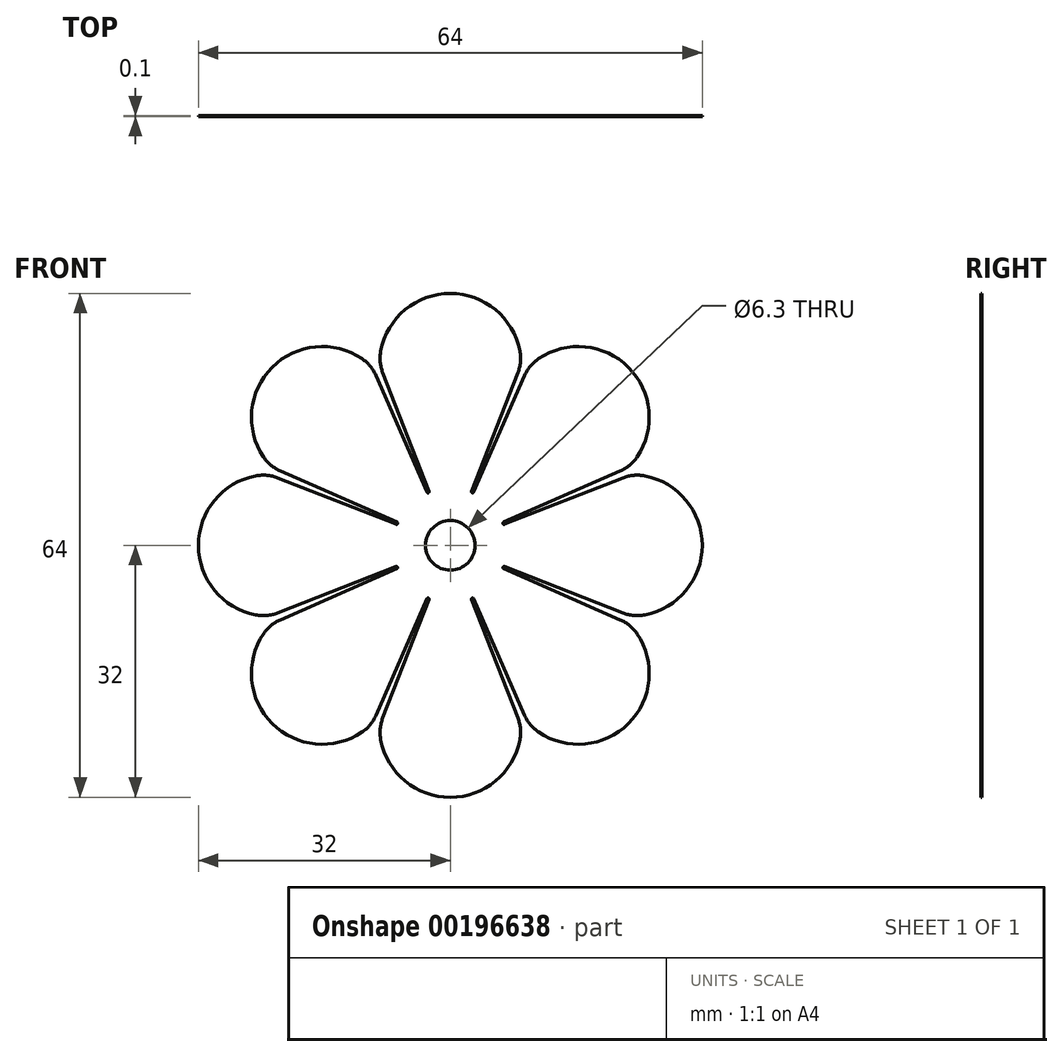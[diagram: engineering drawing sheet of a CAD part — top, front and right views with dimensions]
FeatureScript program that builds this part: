
annotation { "Feature Type Name" : "Feature", "Feature Type Description" : "" }
export const myFeature = defineFeature(function(context is Context, id is Id, definition is map)
    precondition{}
    {
        {
            var Q0;
            Q0=qCreatedBy(makeId("Front.planeOp"),FACE);
            var sketch = newSketch(context, id + "F0", { "sketchPlane" : qUnion([Q0])});
            skCircle(sketch, "E0", {"center": v(0, 0) * mm, "radius": 3.15 * mm});
            skArc(sketch, "E1", {"start": v(-2.77, 6.7) * mm, "mid": v(-2.77, 6.7) * mm, "end": v(-2.78, 6.7) * mm});
            skArc(sketch, "E2", {"start": v(-8.84, 24.7) * mm, "mid": v(0, 32) * mm, "end": v(8.84, 24.7) * mm});
            skLineSegment(sketch, "E3", {"start": v(0, 0) * mm, "end": v(1.15, 2.93) * mm});
            skPoint(sketch, "E4.visualSharp", {"position": v(-9, 23) * mm});
            skArc(sketch, "E4.filletArc", {"start": v(-8.84, 24.7) * mm, "mid": v(-8.9, 23.3) * mm, "end": v(-8.58, 21.94) * mm});
            skPoint(sketch, "E5.visualSharp", {"position": v(9, 23) * mm});
            skArc(sketch, "E5.filletArc", {"start": v(8.58, 21.94) * mm, "mid": v(8.9, 23.3) * mm, "end": v(8.84, 24.7) * mm});
            skLineSegment(sketch, "E6.trimOffspring", {"start": v(-2.7, 6.88) * mm, "end": v(-8.58, 21.94) * mm});
            skLineSegment(sketch, "E7.trimOffspring", {"start": v(2.7, 6.88) * mm, "end": v(8.58, 21.94) * mm});
            skLineSegment(sketch, "E8.1.0", {"start": v(-6.77, 2.96) * mm, "end": v(-21.58, 9.44) * mm});
            skArc(sketch, "E8.1.1", {"start": v(-23.72, 11.22) * mm, "mid": v(-22.78, 10.18) * mm, "end": v(-21.58, 9.44) * mm});
            skArc(sketch, "E8.1.2", {"start": v(-23.72, 11.22) * mm, "mid": v(-22.63, 22.63) * mm, "end": v(-11.22, 23.72) * mm});
            skArc(sketch, "E8.1.3", {"start": v(-9.44, 21.58) * mm, "mid": v(-10.18, 22.78) * mm, "end": v(-11.22, 23.72) * mm});
            skLineSegment(sketch, "E8.1.4", {"start": v(-2.96, 6.77) * mm, "end": v(-9.44, 21.58) * mm});
            skLineSegment(sketch, "E8.2.0", {"start": v(-6.88, -2.7) * mm, "end": v(-21.94, -8.58) * mm});
            skArc(sketch, "E8.2.1", {"start": v(-24.7, -8.84) * mm, "mid": v(-23.3, -8.9) * mm, "end": v(-21.94, -8.58) * mm});
            skArc(sketch, "E8.2.2", {"start": v(-24.7, -8.84) * mm, "mid": v(-32, 0) * mm, "end": v(-24.7, 8.84) * mm});
            skArc(sketch, "E8.2.3", {"start": v(-21.94, 8.58) * mm, "mid": v(-23.3, 8.9) * mm, "end": v(-24.7, 8.84) * mm});
            skLineSegment(sketch, "E8.2.4", {"start": v(-6.88, 2.7) * mm, "end": v(-21.94, 8.58) * mm});
            skLineSegment(sketch, "E8.3.0", {"start": v(-2.96, -6.77) * mm, "end": v(-9.44, -21.58) * mm});
            skArc(sketch, "E8.3.1", {"start": v(-11.22, -23.72) * mm, "mid": v(-10.18, -22.78) * mm, "end": v(-9.44, -21.58) * mm});
            skArc(sketch, "E8.3.2", {"start": v(-11.22, -23.72) * mm, "mid": v(-22.63, -22.63) * mm, "end": v(-23.72, -11.22) * mm});
            skArc(sketch, "E8.3.3", {"start": v(-21.58, -9.44) * mm, "mid": v(-22.78, -10.18) * mm, "end": v(-23.72, -11.22) * mm});
            skLineSegment(sketch, "E8.3.4", {"start": v(-6.77, -2.96) * mm, "end": v(-21.58, -9.44) * mm});
            skLineSegment(sketch, "E8.4.0", {"start": v(2.7, -6.88) * mm, "end": v(8.58, -21.94) * mm});
            skArc(sketch, "E8.4.1", {"start": v(8.84, -24.7) * mm, "mid": v(8.9, -23.3) * mm, "end": v(8.58, -21.94) * mm});
            skArc(sketch, "E8.4.2", {"start": v(8.84, -24.7) * mm, "mid": v(0, -32) * mm, "end": v(-8.84, -24.7) * mm});
            skArc(sketch, "E8.4.3", {"start": v(-8.58, -21.94) * mm, "mid": v(-8.9, -23.3) * mm, "end": v(-8.84, -24.7) * mm});
            skLineSegment(sketch, "E8.4.4", {"start": v(-2.7, -6.88) * mm, "end": v(-8.58, -21.94) * mm});
            skLineSegment(sketch, "E8.5.0", {"start": v(6.77, -2.96) * mm, "end": v(21.58, -9.44) * mm});
            skArc(sketch, "E8.5.1", {"start": v(23.72, -11.22) * mm, "mid": v(22.78, -10.18) * mm, "end": v(21.58, -9.44) * mm});
            skArc(sketch, "E8.5.2", {"start": v(23.72, -11.22) * mm, "mid": v(22.63, -22.63) * mm, "end": v(11.22, -23.72) * mm});
            skArc(sketch, "E8.5.3", {"start": v(9.44, -21.58) * mm, "mid": v(10.18, -22.78) * mm, "end": v(11.22, -23.72) * mm});
            skLineSegment(sketch, "E8.5.4", {"start": v(2.96, -6.77) * mm, "end": v(9.44, -21.58) * mm});
            skLineSegment(sketch, "E8.6.0", {"start": v(6.88, 2.7) * mm, "end": v(21.94, 8.58) * mm});
            skArc(sketch, "E8.6.1", {"start": v(24.7, 8.84) * mm, "mid": v(23.3, 8.9) * mm, "end": v(21.94, 8.58) * mm});
            skArc(sketch, "E8.6.2", {"start": v(24.7, 8.84) * mm, "mid": v(32, 0) * mm, "end": v(24.7, -8.84) * mm});
            skArc(sketch, "E8.6.3", {"start": v(21.94, -8.58) * mm, "mid": v(23.3, -8.9) * mm, "end": v(24.7, -8.84) * mm});
            skLineSegment(sketch, "E8.6.4", {"start": v(6.88, -2.7) * mm, "end": v(21.94, -8.58) * mm});
            skLineSegment(sketch, "E8.7.0", {"start": v(2.96, 6.77) * mm, "end": v(9.44, 21.58) * mm});
            skArc(sketch, "E8.7.1", {"start": v(11.22, 23.72) * mm, "mid": v(10.18, 22.78) * mm, "end": v(9.44, 21.58) * mm});
            skArc(sketch, "E8.7.2", {"start": v(11.22, 23.72) * mm, "mid": v(22.63, 22.63) * mm, "end": v(23.72, 11.22) * mm});
            skArc(sketch, "E8.7.3", {"start": v(21.58, 9.44) * mm, "mid": v(22.78, 10.18) * mm, "end": v(23.72, 11.22) * mm});
            skLineSegment(sketch, "E8.7.4", {"start": v(6.77, 2.96) * mm, "end": v(21.58, 9.44) * mm});
            skArc(sketch, "E9.trimOffspring", {"start": v(-2.78, -6.7) * mm, "mid": v(-2.77, -6.7) * mm, "end": v(-2.77, -6.7) * mm});
            skArc(sketch, "E10.trimOffspring", {"start": v(-6.7, -2.77) * mm, "mid": v(-6.7, -2.77) * mm, "end": v(-6.7, -2.78) * mm});
            skArc(sketch, "E11.trimOffspring", {"start": v(-6.7, 2.78) * mm, "mid": v(-6.7, 2.77) * mm, "end": v(-6.7, 2.77) * mm});
            skArc(sketch, "E12.trimOffspring", {"start": v(2.78, 6.7) * mm, "mid": v(2.77, 6.7) * mm, "end": v(2.77, 6.7) * mm});
            skArc(sketch, "E13.trimOffspring", {"start": v(6.7, 2.77) * mm, "mid": v(6.7, 2.77) * mm, "end": v(6.7, 2.78) * mm});
            skArc(sketch, "E14.trimOffspring", {"start": v(6.7, -2.78) * mm, "mid": v(6.7, -2.77) * mm, "end": v(6.7, -2.77) * mm});
            skArc(sketch, "E15.trimOffspring", {"start": v(2.77, -6.7) * mm, "mid": v(2.77, -6.7) * mm, "end": v(2.78, -6.7) * mm});
            skPoint(sketch, "E16.visualSharp", {"position": v(-2.64, 6.75) * mm});
            skArc(sketch, "E16.filletArc", {"start": v(-2.77, 6.7) * mm, "mid": v(-2.7, 6.77) * mm, "end": v(-2.7, 6.88) * mm});
            skPoint(sketch, "E17.visualSharp", {"position": v(-2.9, 6.64) * mm});
            skArc(sketch, "E17.filletArc", {"start": v(-2.96, 6.77) * mm, "mid": v(-2.89, 6.7) * mm, "end": v(-2.78, 6.7) * mm});
            skPoint(sketch, "E18.visualSharp", {"position": v(-6.64, 2.9) * mm});
            skArc(sketch, "E18.filletArc", {"start": v(-6.7, 2.78) * mm, "mid": v(-6.7, 2.89) * mm, "end": v(-6.77, 2.96) * mm});
            skPoint(sketch, "E19.visualSharp", {"position": v(-6.75, 2.64) * mm});
            skArc(sketch, "E19.filletArc", {"start": v(-6.88, 2.7) * mm, "mid": v(-6.77, 2.7) * mm, "end": v(-6.7, 2.77) * mm});
            skPoint(sketch, "E20.visualSharp", {"position": v(-6.75, -2.64) * mm});
            skArc(sketch, "E20.filletArc", {"start": v(-6.7, -2.77) * mm, "mid": v(-6.77, -2.7) * mm, "end": v(-6.88, -2.7) * mm});
            skPoint(sketch, "E21.visualSharp", {"position": v(-6.64, -2.9) * mm});
            skArc(sketch, "E21.filletArc", {"start": v(-6.77, -2.96) * mm, "mid": v(-6.7, -2.89) * mm, "end": v(-6.7, -2.78) * mm});
            skPoint(sketch, "E22.visualSharp", {"position": v(-2.9, -6.64) * mm});
            skArc(sketch, "E22.filletArc", {"start": v(-2.78, -6.7) * mm, "mid": v(-2.89, -6.7) * mm, "end": v(-2.96, -6.77) * mm});
            skPoint(sketch, "E23.visualSharp", {"position": v(-2.64, -6.75) * mm});
            skArc(sketch, "E23.filletArc", {"start": v(-2.7, -6.88) * mm, "mid": v(-2.7, -6.77) * mm, "end": v(-2.77, -6.7) * mm});
            skPoint(sketch, "E24.visualSharp", {"position": v(2.64, -6.75) * mm});
            skArc(sketch, "E24.filletArc", {"start": v(2.77, -6.7) * mm, "mid": v(2.7, -6.77) * mm, "end": v(2.7, -6.88) * mm});
            skPoint(sketch, "E25.visualSharp", {"position": v(2.9, -6.64) * mm});
            skArc(sketch, "E25.filletArc", {"start": v(2.96, -6.77) * mm, "mid": v(2.89, -6.7) * mm, "end": v(2.78, -6.7) * mm});
            skPoint(sketch, "E26.visualSharp", {"position": v(6.64, -2.9) * mm});
            skArc(sketch, "E26.filletArc", {"start": v(6.7, -2.78) * mm, "mid": v(6.7, -2.89) * mm, "end": v(6.77, -2.96) * mm});
            skPoint(sketch, "E27.visualSharp", {"position": v(6.75, -2.64) * mm});
            skArc(sketch, "E27.filletArc", {"start": v(6.88, -2.7) * mm, "mid": v(6.77, -2.7) * mm, "end": v(6.7, -2.77) * mm});
            skPoint(sketch, "E28.visualSharp", {"position": v(6.75, 2.64) * mm});
            skArc(sketch, "E28.filletArc", {"start": v(6.7, 2.77) * mm, "mid": v(6.77, 2.7) * mm, "end": v(6.88, 2.7) * mm});
            skPoint(sketch, "E29.visualSharp", {"position": v(6.64, 2.9) * mm});
            skArc(sketch, "E29.filletArc", {"start": v(6.77, 2.96) * mm, "mid": v(6.7, 2.89) * mm, "end": v(6.7, 2.78) * mm});
            skPoint(sketch, "E30.visualSharp", {"position": v(2.9, 6.64) * mm});
            skArc(sketch, "E30.filletArc", {"start": v(2.78, 6.7) * mm, "mid": v(2.89, 6.7) * mm, "end": v(2.96, 6.77) * mm});
            skPoint(sketch, "E31.visualSharp", {"position": v(2.64, 6.75) * mm});
            skArc(sketch, "E31.filletArc", {"start": v(2.7, 6.88) * mm, "mid": v(2.7, 6.77) * mm, "end": v(2.77, 6.7) * mm});
            skSolve(sketch);
        }
        {
            var Q0;
            Q0=makeQuery(id+"F0.imprint","IMPRINT",FACE,{"disambiguationData":[TD([[makeQuery(id+"F0.imprint","IMPRINT",EDGE,{"derivedFrom":sQuery(id+"F0.wireOp",EDGE,"E0")}),-1.0]])]});
            extrude(context, id + "F1", {"entities" : qUnion([Q0]), "endBound" : BoundingType.SYMMETRIC, "depth" : .1 * mm});
        }
    });
